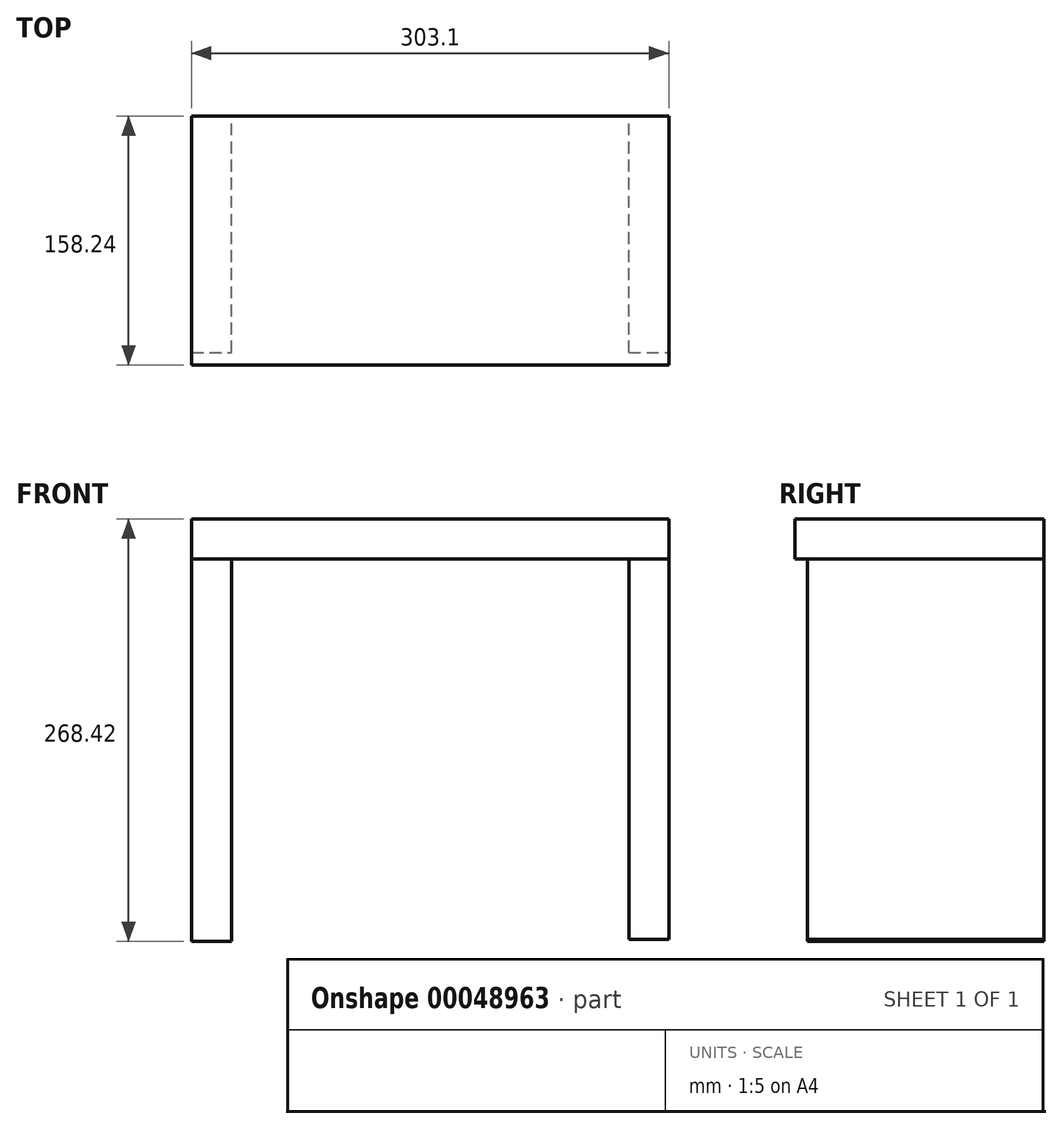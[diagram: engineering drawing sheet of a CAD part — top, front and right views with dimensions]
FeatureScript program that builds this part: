
annotation { "Feature Type Name" : "Feature", "Feature Type Description" : "" }
export const myFeature = defineFeature(function(context is Context, id is Id, definition is map)
    precondition{}
    {
        {
            var Q0;
            Q0=qCreatedBy(makeId("Top.planeOp"),FACE);
            var sketch = newSketch(context, id + "F0", { "sketchPlane" : qUnion([Q0])});
            skLineSegment(sketch, "E0.rect.bottom", {"start": v(0, -8.1) * mm, "end": v(-302.95, -8.1) * mm});
            skLineSegment(sketch, "E0.rect.top", {"start": v(0, 150.14) * mm, "end": v(-302.95, 150.14) * mm});
            skLineSegment(sketch, "E0.rect.left", {"start": v(0, -8.1) * mm, "end": v(0, 150.14) * mm});
            skLineSegment(sketch, "E0.rect.right", {"start": v(-302.95, -8.1) * mm, "end": v(-302.95, 150.14) * mm});
            skPoint(sketch, "E0.rect.middle", {"position": v(-151.47, 71.02) * mm});
            skSolve(sketch);
        }
        {
            var Q0;
            Q0 = qSketchRegion(id + "F0", true);
            extrude(context, id + "F1", {"entities" : qUnion([Q0]), "depth" : 25.4 * mm});
        }
        {
            var Q0;
            Q0=qCreatedBy(makeId("Right.planeOp"),FACE);
            var sketch = newSketch(context, id + "F2", { "sketchPlane" : qUnion([Q0])});
            skLineSegment(sketch, "E1.bottom", {"start": v(0, 0) * mm, "end": v(150.1, 0) * mm});
            skLineSegment(sketch, "E1.top", {"start": v(0, -241.83) * mm, "end": v(150.1, -241.83) * mm});
            skLineSegment(sketch, "E1.left", {"start": v(0, 0) * mm, "end": v(0, -241.83) * mm});
            skLineSegment(sketch, "E1.right", {"start": v(150.1, 0) * mm, "end": v(150.1, -241.83) * mm});
            skSolve(sketch);
        }
        {
            var Q0;
            Q0=makeQuery(id+"F2.imprint","IMPRINT",FACE,{"disambiguationData":[TD([[makeQuery(id+"F2.imprint","IMPRINT",EDGE,{"derivedFrom":sQuery(id+"F2.wireOp",EDGE,"E1.bottom")}),-1.0]])]});
            extrude(context, id + "F3", {"entities" : qUnion([Q0]), "oppositeDirection" : true, "depth" : 25.4 * mm});
        }
        {
            var Q0;
            Q0=qCreatedBy(makeId("Right.planeOp"),FACE);
            var sketch = newSketch(context, id + "F4", { "sketchPlane" : qUnion([Q0])});
            skLineSegment(sketch, "E2.bottom", {"start": v(0, 0) * mm, "end": v(149.99, 0) * mm});
            skLineSegment(sketch, "E2.top", {"start": v(0, -243.02) * mm, "end": v(149.99, -243.02) * mm});
            skLineSegment(sketch, "E2.left", {"start": v(0, 0) * mm, "end": v(0, -243.02) * mm});
            skLineSegment(sketch, "E2.right", {"start": v(149.99, 0) * mm, "end": v(149.99, -243.02) * mm});
            skSolve(sketch);
        }
        {
            var Q0;
            Q0=makeQuery(id+"F4.imprint","IMPRINT",FACE,{"disambiguationData":[TD([[makeQuery(id+"F4.imprint","IMPRINT",EDGE,{"derivedFrom":sQuery(id+"F4.wireOp",EDGE,"E2.bottom")}),-1.0]])]});
            extrude(context, id + "F5", {"entities" : qUnion([Q0]), "operationType" : NewBodyOperationType.ADD, "oppositeDirection" : true, "depth" : 303.1 * mm, "hasSecondDirection" : true, "secondDirectionOppositeDirection" : true, "secondDirectionDepth" : 277.64 * mm});
        }
    });
